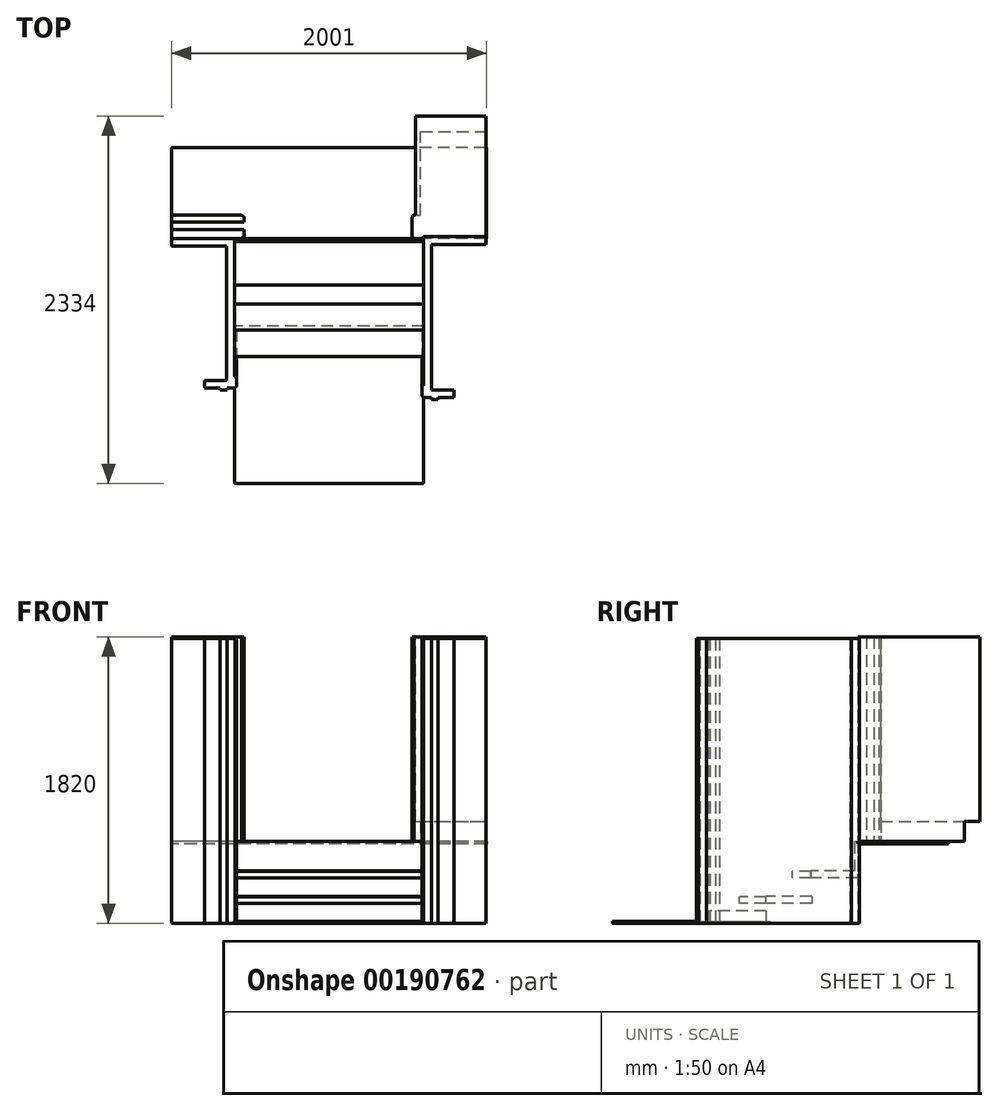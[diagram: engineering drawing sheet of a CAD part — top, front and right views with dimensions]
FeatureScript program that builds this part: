
annotation { "Feature Type Name" : "Feature", "Feature Type Description" : "" }
export const myFeature = defineFeature(function(context is Context, id is Id, definition is map)
    precondition{}
    {
        {
            var Q0;
            Q0=qCreatedBy(makeId("Right.planeOp"),FACE);
            var sketch = newSketch(context, id + "F0", { "sketchPlane" : qUnion([Q0])});
            skLineSegment(sketch, "E0.bottom", {"start": v(0, 0) * mm, "end": v(20, 0) * mm});
            skLineSegment(sketch, "E0.top", {"start": v(0, -187) * mm, "end": v(20, -187) * mm});
            skLineSegment(sketch, "E0.left", {"start": v(0, 0) * mm, "end": v(0, -187) * mm});
            skLineSegment(sketch, "E0.right", {"start": v(20, 0) * mm, "end": v(20, -187) * mm});
            skLineSegment(sketch, "E1.bottom", {"start": v(20, -187) * mm, "end": v(-276, -187) * mm});
            skLineSegment(sketch, "E1.top", {"start": v(20, -230) * mm, "end": v(-276, -230) * mm});
            skLineSegment(sketch, "E1.left", {"start": v(20, -187) * mm, "end": v(20, -230) * mm});
            skLineSegment(sketch, "E1.right", {"start": v(-276, -187) * mm, "end": v(-276, -230) * mm});
            skLineSegment(sketch, "E2.bottom", {"start": v(-272, -230) * mm, "end": v(-252, -230) * mm});
            skLineSegment(sketch, "E2.top", {"start": v(-272, -391) * mm, "end": v(-252, -391) * mm});
            skLineSegment(sketch, "E2.left", {"start": v(-272, -230) * mm, "end": v(-272, -391) * mm});
            skLineSegment(sketch, "E2.right", {"start": v(-252, -230) * mm, "end": v(-252, -391) * mm});
            skLineSegment(sketch, "E3.bottom", {"start": v(-272, -391) * mm, "end": v(-562, -391) * mm});
            skLineSegment(sketch, "E3.top", {"start": v(-272, -348) * mm, "end": v(-562, -348) * mm});
            skLineSegment(sketch, "E3.left", {"start": v(-272, -391) * mm, "end": v(-272, -348) * mm});
            skLineSegment(sketch, "E3.right", {"start": v(-562, -391) * mm, "end": v(-562, -348) * mm});
            skLineSegment(sketch, "E4.bottom", {"start": v(-557, -391) * mm, "end": v(-537, -391) * mm});
            skLineSegment(sketch, "E4.top", {"start": v(-557, -505) * mm, "end": v(-537, -505) * mm});
            skLineSegment(sketch, "E4.left", {"start": v(-557, -391) * mm, "end": v(-557, -505) * mm});
            skLineSegment(sketch, "E4.right", {"start": v(-537, -391) * mm, "end": v(-537, -505) * mm});
            skLineSegment(sketch, "E5.bottom", {"start": v(20, 0) * mm, "end": v(597, 0) * mm});
            skLineSegment(sketch, "E5.top", {"start": v(20, -15) * mm, "end": v(597, -15) * mm});
            skLineSegment(sketch, "E5.left", {"start": v(20, 0) * mm, "end": v(20, -15) * mm});
            skLineSegment(sketch, "E5.right", {"start": v(597, 0) * mm, "end": v(597, -15) * mm});
            skLineSegment(sketch, "E6.bottom", {"start": v(-537, -505) * mm, "end": v(-1537, -505) * mm});
            skLineSegment(sketch, "E6.top", {"start": v(-537, -520) * mm, "end": v(-1537, -520) * mm});
            skLineSegment(sketch, "E6.left", {"start": v(-537, -505) * mm, "end": v(-537, -520) * mm});
            skLineSegment(sketch, "E6.right", {"start": v(-1537, -505) * mm, "end": v(-1537, -520) * mm});
            skSolve(sketch);
        }
        {
            var Q0;
            Q0=makeQuery(id+"F0.imprint","IMPRINT",FACE,{"disambiguationData":[TD([[makeQuery(id+"F0.imprint","IMPRINT",EDGE,{"derivedFrom":sQuery(id+"F0.wireOp",EDGE,"E0.bottom")}),-1.0]])]});
            var Q1;
            {var subQ3=sQuery(id+"F0.wireOp",EDGE,"E1.left");Q1=makeQuery(id+"F0.imprint","IMPRINT",FACE,{"disambiguationData":[TD([[makeQuery(id+"F0.imprint","IMPRINT",EDGE,{"derivedFrom":subQ3}),-1.0]])]});}
            var Q2;
            Q2=makeQuery(id+"F0.imprint","IMPRINT",FACE,{"disambiguationData":[TD([[makeQuery(id+"F0.imprint","IMPRINT",EDGE,{"derivedFrom":sQuery(id+"F0.wireOp",EDGE,"E2.bottom")}),-1.0]])]});
            var Q3;
            Q3=makeQuery(id+"F0.imprint","IMPRINT",FACE,{"disambiguationData":[TD([[makeQuery(id+"F0.imprint","IMPRINT",EDGE,{"derivedFrom":sQuery(id+"F0.wireOp",EDGE,"E3.top")}),1.0]])]});
            var Q4;
            Q4=makeQuery(id+"F0.imprint","IMPRINT",FACE,{"disambiguationData":[TD([[makeQuery(id+"F0.imprint","IMPRINT",EDGE,{"derivedFrom":sQuery(id+"F0.wireOp",EDGE,"E4.bottom")}),-1.0]])]});
            extrude(context, id + "F1", {"entities" : qUnion([Q0, Q1, Q2, Q3, Q4]), "endBound" : BoundingType.SYMMETRIC, "depth" : 1200 * mm, "hasSecondDirection" : true, "secondDirectionOppositeDirection" : true, "secondDirectionDepth" : 25 * mm});
        }
        {
            var Q0;
            Q0=makeQuery(id+"F0.imprint","IMPRINT",FACE,{"disambiguationData":[TD([[makeQuery(id+"F0.imprint","IMPRINT",EDGE,{"derivedFrom":sQuery(id+"F0.wireOp",EDGE,"E6.top")}),-1.0]])]});
            extrude(context, id + "F2", {"entities" : qUnion([Q0]), "endBound" : BoundingType.SYMMETRIC, "depth" : 1200 * mm});
        }
        {
            var Q0;
            Q0=makeQuery(id+"F0.imprint","IMPRINT",FACE,{"disambiguationData":[TD([[makeQuery(id+"F0.imprint","IMPRINT",EDGE,{"derivedFrom":sQuery(id+"F0.wireOp",EDGE,"E5.bottom")}),-1.0]])]});
            extrude(context, id + "F3", {"entities" : qUnion([Q0]), "endBound" : BoundingType.SYMMETRIC, "depth" : 2000 * mm});
        }
        {
            var Q0;
            Q0=makeQuery(id+"F3.opExtrude","SWEPT_FACE",FACE,{"disambiguationData":[OSD([sQuery(id+"F0.wireOp",EDGE,"E5.bottom")])]});
            var sketch = newSketch(context, id + "F4", { "sketchPlane" : qUnion([Q0])});
            skLineSegment(sketch, "E7.bottom", {"start": v(600, 20) * mm, "end": v(540, 20) * mm});
            skLineSegment(sketch, "E7.top", {"start": v(600, 31) * mm, "end": v(530, 31) * mm});
            skLineSegment(sketch, "E7.left", {"start": v(600, 20) * mm, "end": v(600, 31) * mm});
            skLineSegment(sketch, "E7.right", {"start": v(530, 28) * mm, "end": v(530, 31) * mm});
            skLineSegment(sketch, "E8", {"start": v(540, 20) * mm, "end": v(530, 28) * mm});
            skLineSegment(sketch, "E9", {"start": v(530, 31) * mm, "end": v(525, 31) * mm});
            skLineSegment(sketch, "E10", {"start": v(525, 31) * mm, "end": v(525, 156) * mm});
            skLineSegment(sketch, "E11", {"start": v(525, 156) * mm, "end": v(530, 156) * mm});
            skLineSegment(sketch, "E12", {"start": v(530, 156) * mm, "end": v(530, 164) * mm});
            skLineSegment(sketch, "E13", {"start": v(530, 164) * mm, "end": v(540, 167) * mm});
            skLineSegment(sketch, "E14", {"start": v(540, 167) * mm, "end": v(580, 167) * mm});
            skLineSegment(sketch, "E15", {"start": v(580, 167) * mm, "end": v(580, 697) * mm});
            skLineSegment(sketch, "E16", {"start": v(580, 697) * mm, "end": v(995, 697) * mm});
            skLineSegment(sketch, "E17", {"start": v(995, 697) * mm, "end": v(995, 31) * mm});
            skLineSegment(sketch, "E18", {"start": v(995, 31) * mm, "end": v(600, 31) * mm});
            skLineSegment(sketch, "E19", {"start": v(-600, 20) * mm, "end": v(-556, 20) * mm});
            skLineSegment(sketch, "E20", {"start": v(-556, 20) * mm, "end": v(-546, 28) * mm});
            skLineSegment(sketch, "E21", {"start": v(-546, 28) * mm, "end": v(-546, 31) * mm});
            skLineSegment(sketch, "E22", {"start": v(-546, 31) * mm, "end": v(-541, 31) * mm});
            skLineSegment(sketch, "E23", {"start": v(-541, 31) * mm, "end": v(-541, 76) * mm});
            skLineSegment(sketch, "E24", {"start": v(-541, 76) * mm, "end": v(-1001, 76) * mm});
            skLineSegment(sketch, "E25", {"start": v(-1001, 76) * mm, "end": v(-1001, 20) * mm});
            skLineSegment(sketch, "E26", {"start": v(-541, 76) * mm, "end": v(-541, 124) * mm, "construction": true});
            skLineSegment(sketch, "E27", {"start": v(-1001, 20) * mm, "end": v(-556, 20) * mm});
            skPoint(sketch, "E28.endSnap0", {"position": v(-541, 100) * mm});
            skLineSegment(sketch, "E29.MirrorCS", {"start": v(-546, 157) * mm, "end": v(-541, 157) * mm});
            skLineSegment(sketch, "E30.MirrorCS", {"start": v(-556, 168) * mm, "end": v(-546, 160) * mm});
            skLineSegment(sketch, "E31.MirrorCS", {"start": v(-546, 160) * mm, "end": v(-546, 157) * mm});
            skLineSegment(sketch, "E32.MirrorCS", {"start": v(-600, 168) * mm, "end": v(-556, 168) * mm});
            skLineSegment(sketch, "E33.MirrorCS", {"start": v(-541, 124) * mm, "end": v(-1001, 124) * mm});
            skLineSegment(sketch, "E34.MirrorCS", {"start": v(-1001, 168) * mm, "end": v(-556, 168) * mm});
            skLineSegment(sketch, "E35.MirrorCS", {"start": v(-1001, 124) * mm, "end": v(-1001, 168) * mm});
            skLineSegment(sketch, "E36.MirrorCS", {"start": v(-541, 157) * mm, "end": v(-541, 124) * mm});
            skLineSegment(sketch, "E37", {"start": v(-556, 20) * mm, "end": v(-556, 168) * mm, "construction": true});
            skLineSegment(sketch, "E38", {"start": v(-546, 31) * mm, "end": v(-546, 157) * mm, "construction": true});
            skLineSegment(sketch, "E39", {"start": v(-1001, 76) * mm, "end": v(-1001, 124) * mm, "construction": true});
            skLineSegment(sketch, "E40", {"start": v(580, 167) * mm, "end": v(995, 167) * mm});
            skSolve(sketch);
        }
        {
            var Q0;
            {var subQ0=sQuery(id+"F4.wireOp",EDGE,"E20");Q0=makeQuery(id+"F4.imprint","IMPRINT",FACE,{"disambiguationData":[TD([[makeQuery(id+"F4.imprint","IMPRINT",EDGE,{"derivedFrom":subQ0}),1.0]])]});}
            var Q1;
            Q1=makeQuery(id+"F4.imprint","IMPRINT",FACE,{"disambiguationData":[TD([[makeQuery(id+"F4.imprint","IMPRINT",EDGE,{"derivedFrom":sQuery(id+"F4.wireOp",EDGE,"E29.MirrorCS")}),-1.0]])]});
            var Q2;
            Q2=makeQuery(id+"F4.imprint","IMPRINT",FACE,{"disambiguationData":[TD([[makeQuery(id+"F4.imprint","IMPRINT",EDGE,{"derivedFrom":sQuery(id+"F4.wireOp",EDGE,"E7.top")}),-1.0]])]});
            var Q3;
            {var subQ0=sQuery(id+"F4.wireOp",EDGE,"E40");Q3=makeQuery(id+"F4.imprint","IMPRINT",FACE,{"disambiguationData":[TD([[makeQuery(id+"F4.imprint","IMPRINT",EDGE,{"derivedFrom":subQ0}),1.0]])]});}
            var Q4;
            {var subQ0=sQuery(id+"F4.wireOp",EDGE,"E16");Q4=makeQuery(id+"F4.imprint","IMPRINT",FACE,{"disambiguationData":[TD([[makeQuery(id+"F4.imprint","IMPRINT",EDGE,{"derivedFrom":subQ0}),-1.0]])]});}
            var Q5;
            Q5=makeQuery(id+"F4.imprint","IMPRINT",FACE,{"disambiguationData":[TD([[makeQuery(id+"F4.imprint","IMPRINT",EDGE,{"derivedFrom":sQuery(id+"F4.wireOp",EDGE,"E7.bottom")}),-1.0]])]});
            extrude(context, id + "F5", {"entities" : qUnion([Q0, Q1, Q2, Q3, Q4, Q5]), "depth" : 1300 * mm});
        }
        {
            var Q0;
            Q0=makeQuery(id+"F5.opExtrude","CAP_FACE",FACE,{"disambiguationData":[OSD([sQuery(id+"F4.wireOp",EDGE,"E7.top"),sQuery(id+"F4.wireOp",EDGE,"E9"),sQuery(id+"F4.wireOp",EDGE,"E10"),sQuery(id+"F4.wireOp",EDGE,"E11"),sQuery(id+"F4.wireOp",EDGE,"E12"),sQuery(id+"F4.wireOp",EDGE,"E13"),sQuery(id+"F4.wireOp",EDGE,"E14"),sQuery(id+"F4.wireOp",EDGE,"E15"),sQuery(id+"F4.wireOp",EDGE,"E16"),sQuery(id+"F4.wireOp",EDGE,"E17"),sQuery(id+"F4.wireOp",EDGE,"E18")])],"isStart":false});
            var sketch = newSketch(context, id + "F6", { "sketchPlane" : qUnion([Q0])});
            skLineSegment(sketch, "E41", {"start": v(550, 167) * mm, "end": v(550, 797) * mm});
            skLineSegment(sketch, "E42", {"start": v(550, 797) * mm, "end": v(995, 797) * mm});
            skLineSegment(sketch, "E43", {"start": v(995, 797) * mm, "end": v(995, 164) * mm});
            skLineSegment(sketch, "E44", {"start": v(995, 164) * mm, "end": v(550, 167) * mm});
            skSolve(sketch);
        }
        {
            var Q0;
            {var subQ4=sQuery(id+"F6.wireOp",EDGE,"E41");Q0=makeQuery(id+"F6.imprint","IMPRINT",FACE,{"disambiguationData":[TD([[makeQuery(id+"F6.imprint","IMPRINT",EDGE,{"derivedFrom":subQ4}),-1.0]])]});}
            extrude(context, id + "F7", {"entities" : qUnion([Q0]), "operationType" : NewBodyOperationType.ADD, "oppositeDirection" : true, "depth" : 1170 * mm});
        }
        {
            var Q0;
            Q0=makeQuery(id+"F2.opExtrude","SWEPT_FACE",FACE,{"disambiguationData":[OSD([sQuery(id+"F0.wireOp",EDGE,"E6.top")])]});
            cPlane(context, id + "F8", {"entities" : qUnion([Q0]), "cplaneType" : CPlaneType.OFFSET, "offset" : 0 * mm, "width" : 150 * mm, "height" : 150 * mm});
        }
        {
            var Q0;
            Q0=qCreatedBy(id+"F8.planeOp",FACE);
            var sketch = newSketch(context, id + "F9", { "sketchPlane" : qUnion([Q0])});
            skLineSegment(sketch, "E45.0", {"start": v(995, -31) * mm, "end": v(600, -31) * mm});
            skLineSegment(sketch, "E46", {"start": v(600, -31) * mm, "end": v(600, 917) * mm});
            skLineSegment(sketch, "E47", {"start": v(600, 917) * mm, "end": v(589, 917) * mm});
            skLineSegment(sketch, "E48", {"start": v(589, 917) * mm, "end": v(589, 982) * mm});
            skLineSegment(sketch, "E49", {"start": v(589, 982) * mm, "end": v(599, 989) * mm});
            skLineSegment(sketch, "E50", {"start": v(599, 989) * mm, "end": v(599, 992) * mm});
            skLineSegment(sketch, "E51", {"start": v(599, 992) * mm, "end": v(649, 992) * mm});
            skLineSegment(sketch, "E52", {"start": v(649, 992) * mm, "end": v(649, 1005) * mm});
            skLineSegment(sketch, "E53", {"start": v(649, 1005) * mm, "end": v(692, 1005) * mm});
            skLineSegment(sketch, "E54", {"start": v(692, 1005) * mm, "end": v(692, 992) * mm});
            skLineSegment(sketch, "E55", {"start": v(692, 992) * mm, "end": v(792, 992) * mm});
            skLineSegment(sketch, "E56", {"start": v(792, 992) * mm, "end": v(792, 942) * mm});
            skLineSegment(sketch, "E57", {"start": v(792, 942) * mm, "end": v(650, 942) * mm});
            skLineSegment(sketch, "E58", {"start": v(650, 942) * mm, "end": v(650, 19) * mm});
            skLineSegment(sketch, "E59", {"start": v(650, 19) * mm, "end": v(995, 19) * mm});
            skLineSegment(sketch, "E60", {"start": v(995, 19) * mm, "end": v(995, -31) * mm});
            skPoint(sketch, "E61.0", {"position": v(600, 562) * mm});
            skLineSegment(sketch, "E62", {"start": v(600, 562) * mm, "end": v(589, 562) * mm});
            skLineSegment(sketch, "E63", {"start": v(589, 562) * mm, "end": v(589, 917) * mm});
            skPoint(sketch, "E64.0", {"position": v(-1001, -20) * mm});
            skPoint(sketch, "E65.0", {"position": v(-600, -20) * mm});
            skLineSegment(sketch, "E66", {"start": v(-1001, -20) * mm, "end": v(-600, -20) * mm});
            skLineSegment(sketch, "E67", {"start": v(-600, 857) * mm, "end": v(-589, 857) * mm});
            skLineSegment(sketch, "E68", {"start": v(-589, 857) * mm, "end": v(-589, 922) * mm});
            skLineSegment(sketch, "E69", {"start": v(-589, 922) * mm, "end": v(-599, 929) * mm});
            skLineSegment(sketch, "E70", {"start": v(-599, 929) * mm, "end": v(-599, 932) * mm});
            skLineSegment(sketch, "E71", {"start": v(-599, 932) * mm, "end": v(-649, 932) * mm});
            skLineSegment(sketch, "E72", {"start": v(-649, 932) * mm, "end": v(-649, 945) * mm});
            skLineSegment(sketch, "E73", {"start": v(-649, 945) * mm, "end": v(-692, 945) * mm});
            skLineSegment(sketch, "E74", {"start": v(-692, 945) * mm, "end": v(-692, 932) * mm});
            skLineSegment(sketch, "E75", {"start": v(-692, 932) * mm, "end": v(-792, 932) * mm});
            skLineSegment(sketch, "E76", {"start": v(-792, 932) * mm, "end": v(-792, 882) * mm});
            skLineSegment(sketch, "E77", {"start": v(-792, 882) * mm, "end": v(-650, 882) * mm});
            skLineSegment(sketch, "E78", {"start": v(-650, 882) * mm, "end": v(-650, 30) * mm});
            skLineSegment(sketch, "E79", {"start": v(-650, 30) * mm, "end": v(-1001, 30) * mm});
            skLineSegment(sketch, "E80", {"start": v(-1001, 30) * mm, "end": v(-1001, -20) * mm});
            skPoint(sketch, "E81.0", {"position": v(-600, 562) * mm});
            skLineSegment(sketch, "E82", {"start": v(-600, 562) * mm, "end": v(-589, 562) * mm});
            skLineSegment(sketch, "E83", {"start": v(-589, 562) * mm, "end": v(-589, 857) * mm});
            skLineSegment(sketch, "E84", {"start": v(-600, -20) * mm, "end": v(-600, 857) * mm});
            skSolve(sketch);
        }
        {
            var Q0;
            {var subQ1=sQuery(id+"F9.wireOp",EDGE,"E45.0");Q0=makeQuery(id+"F9.imprint","IMPRINT",FACE,{"disambiguationData":[TD([[makeQuery(id+"F9.imprint","IMPRINT",EDGE,{"derivedFrom":subQ1}),-1.0]])]});}
            var Q1;
            {var subQ0=sQuery(id+"F9.wireOp",EDGE,"E66");Q1=makeQuery(id+"F9.imprint","IMPRINT",FACE,{"disambiguationData":[TD([[makeQuery(id+"F9.imprint","IMPRINT",EDGE,{"derivedFrom":subQ0}),1.0]])]});}
            extrude(context, id + "F10", {"entities" : qUnion([Q0, Q1]), "oppositeDirection" : true, "depth" : 1810 * mm});
        }
        {
            var Q0;
            {var subQ0=sQuery(id+"F9.wireOp",EDGE,"E47");Q0=makeQuery(id+"F9.imprint","IMPRINT",FACE,{"disambiguationData":[TD([[makeQuery(id+"F9.imprint","IMPRINT",EDGE,{"derivedFrom":subQ0}),1.0]])]});}
            var Q1;
            {var subQ0=sQuery(id+"F9.wireOp",EDGE,"E67");Q1=makeQuery(id+"F9.imprint","IMPRINT",FACE,{"disambiguationData":[TD([[makeQuery(id+"F9.imprint","IMPRINT",EDGE,{"derivedFrom":subQ0}),-1.0]])]});}
            extrude(context, id + "F11", {"entities" : qUnion([Q0, Q1]), "oppositeDirection" : true, "depth" : 80 * mm});
        }
        {
            var Q0;
            Q0=makeQuery(id+"F10.opExtrude","SWEPT_FACE",FACE,{"disambiguationData":[OSD([sQuery(id+"F9.wireOp",EDGE,"E84")])]});
            var sketch = newSketch(context, id + "F12", { "sketchPlane" : qUnion([Q0])});
            skLineSegment(sketch, "E85", {"start": v(0, 0) * mm, "end": v(-1082.98, -505) * mm, "construction": true});
            skLineSegment(sketch, "E86", {"start": v(-1082.98, -505) * mm, "end": v(-1082.98, 0) * mm, "construction": true});
            skLineSegment(sketch, "E87", {"start": v(-1082.98, 0) * mm, "end": v(0, 0) * mm, "construction": true});
            skPoint(sketch, "E88.0", {"position": v(0, -187) * mm});
            skLineSegment(sketch, "E89.0", {"start": v(-562, -505) * mm, "end": v(-562, -348) * mm});
            skLineSegment(sketch, "E90.0", {"start": v(-537, -505) * mm, "end": v(-1537, -505) * mm});
            skPoint(sketch, "E91.orphan", {"position": v(-276, -230) * mm});
            skPoint(sketch, "E92.orphan", {"position": v(-562, -391) * mm});
            skPoint(sketch, "E93.orphan", {"position": v(-272, -348) * mm});
            skLineSegment(sketch, "E94", {"start": v(-562, -505) * mm, "end": v(-1082.98, -505) * mm, "construction": true});
            skLineSegment(sketch, "E95", {"start": v(-276, -230) * mm, "end": v(-276, -348) * mm});
            skLineSegment(sketch, "E96.bottom", {"start": v(-276, -230) * mm, "end": v(-396, -230) * mm});
            skLineSegment(sketch, "E96.top", {"start": v(-276, -190) * mm, "end": v(-396, -190) * mm});
            skLineSegment(sketch, "E96.left", {"start": v(-276, -230) * mm, "end": v(-276, -190) * mm});
            skLineSegment(sketch, "E96.right", {"start": v(-396, -230) * mm, "end": v(-396, -190) * mm});
            skLineSegment(sketch, "E97.bottom", {"start": v(-562, -391) * mm, "end": v(-732, -391) * mm});
            skLineSegment(sketch, "E97.top", {"start": v(-562, -351) * mm, "end": v(-732, -351) * mm});
            skLineSegment(sketch, "E97.left", {"start": v(-562, -391) * mm, "end": v(-562, -351) * mm});
            skLineSegment(sketch, "E97.right", {"start": v(-732, -391) * mm, "end": v(-732, -351) * mm});
            skLineSegment(sketch, "E98.bottom", {"start": v(-391, -230) * mm, "end": v(-371, -230) * mm});
            skLineSegment(sketch, "E98.top", {"start": v(-391, -348) * mm, "end": v(-371, -348) * mm});
            skLineSegment(sketch, "E98.left", {"start": v(-391, -230) * mm, "end": v(-391, -348) * mm});
            skLineSegment(sketch, "E98.right", {"start": v(-371, -230) * mm, "end": v(-371, -348) * mm});
            skLineSegment(sketch, "E99.bottom", {"start": v(-727, -391) * mm, "end": v(-707, -391) * mm});
            skLineSegment(sketch, "E99.top", {"start": v(-727, -505) * mm, "end": v(-707, -505) * mm});
            skLineSegment(sketch, "E99.left", {"start": v(-727, -391) * mm, "end": v(-727, -505) * mm});
            skLineSegment(sketch, "E99.right", {"start": v(-707, -391) * mm, "end": v(-707, -505) * mm});
            skSolve(sketch);
        }
        {
            var Q0;
            Q0=makeQuery(id+"F12.imprint","IMPRINT",FACE,{"disambiguationData":[TD([[makeQuery(id+"F12.imprint","IMPRINT",EDGE,{"derivedFrom":sQuery(id+"F12.wireOp",EDGE,"E96.bottom")}),-1.0]])]});
            var Q1;
            Q1=makeQuery(id+"F12.imprint","IMPRINT",FACE,{"disambiguationData":[TD([[makeQuery(id+"F12.imprint","IMPRINT",EDGE,{"derivedFrom":sQuery(id+"F12.wireOp",EDGE,"E97.bottom")}),-1.0]])]});
            var Q2;
            Q2=makeQuery(id+"F12.imprint","IMPRINT",FACE,{"disambiguationData":[TD([[makeQuery(id+"F12.imprint","IMPRINT",EDGE,{"derivedFrom":sQuery(id+"F12.wireOp",EDGE,"E99.bottom")}),-1.0]])]});
            var Q3;
            Q3=makeQuery(id+"F12.imprint","IMPRINT",FACE,{"disambiguationData":[TD([[makeQuery(id+"F12.imprint","IMPRINT",EDGE,{"derivedFrom":sQuery(id+"F12.wireOp",EDGE,"E98.bottom")}),-1.0]])]});
            extrude(context, id + "F13", {"entities" : qUnion([Q0, Q1, Q2, Q3]), "depth" : 1200 * mm});
        }
        {
            var Q0;
            Q0=makeQuery(id+"F11.opExtrude","SWEPT_BODY",BODY,{"disambiguationData":[OSD([sQuery(id+"F9.wireOp",EDGE,"E67"),sQuery(id+"F9.wireOp",EDGE,"E82"),sQuery(id+"F9.wireOp",EDGE,"E83"),sQuery(id+"F9.wireOp",EDGE,"E84")])]});
            var Q1;
            Q1=makeQuery(id+"F11.opExtrude","SWEPT_BODY",BODY,{"disambiguationData":[OSD([sQuery(id+"F9.wireOp",EDGE,"E46"),sQuery(id+"F9.wireOp",EDGE,"E47"),sQuery(id+"F9.wireOp",EDGE,"E62"),sQuery(id+"F9.wireOp",EDGE,"E63")])]});
            var Q2;
            Q2=makeQuery(id+"F13.opExtrude","SWEPT_BODY",BODY,{"disambiguationData":[OSD([sQuery(id+"F12.wireOp",EDGE,"E97.bottom"),sQuery(id+"F12.wireOp",EDGE,"E97.top"),sQuery(id+"F12.wireOp",EDGE,"E97.left"),sQuery(id+"F12.wireOp",EDGE,"E97.right"),sQuery(id+"F12.wireOp",EDGE,"E99.top"),sQuery(id+"F12.wireOp",EDGE,"E99.left"),sQuery(id+"F12.wireOp",EDGE,"E99.right")])]});
            booleanBodies(context, id + "F14", {"operationType" : BooleanOperationType.SUBTRACTION, "tools" : qUnion([Q0, Q1]), "targets" : qUnion([Q2]), "keepTools" : true});
        }
    });
